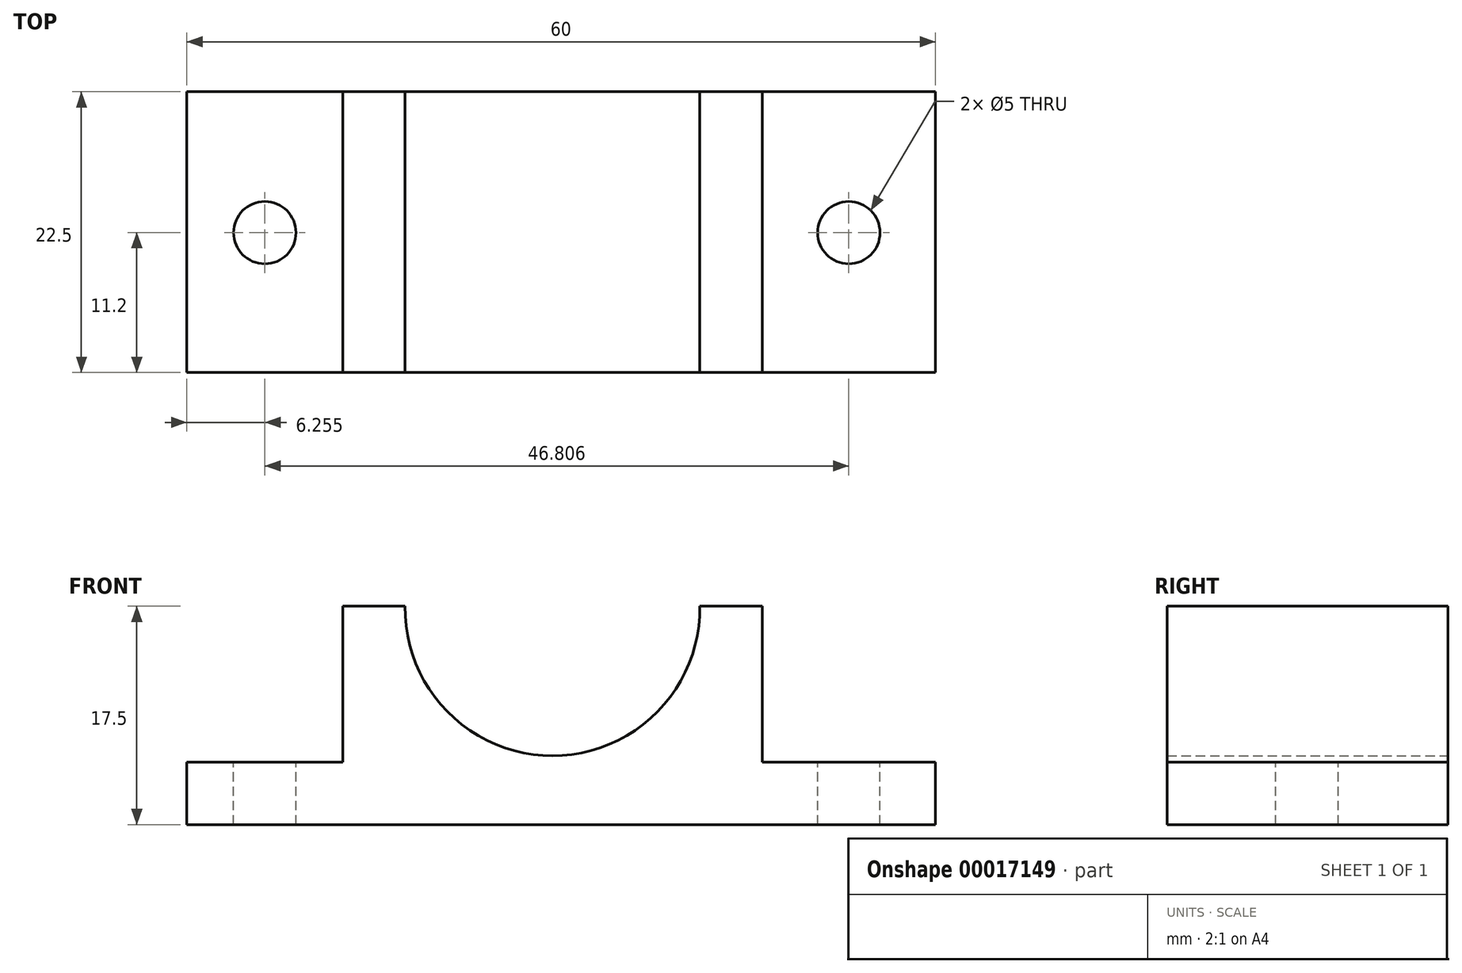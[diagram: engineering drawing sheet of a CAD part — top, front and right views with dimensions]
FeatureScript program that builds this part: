
annotation { "Feature Type Name" : "Feature", "Feature Type Description" : "" }
export const myFeature = defineFeature(function(context is Context, id is Id, definition is map)
    precondition{}
    {
        {
            var Q0;
            Q0=qCreatedBy(makeId("Front.planeOp"),FACE);
            var sketch = newSketch(context, id + "F0", { "sketchPlane" : qUnion([Q0])});
            skLineSegment(sketch, "E0", {"start": v(-45.96, -17.5) * mm, "end": v(14.04, -17.5) * mm});
            skLineSegment(sketch, "E1", {"start": v(14.04, -17.5) * mm, "end": v(14.04, -12.5) * mm});
            skLineSegment(sketch, "E2", {"start": v(14.04, -12.5) * mm, "end": v(0.16, -12.5) * mm});
            skLineSegment(sketch, "E3", {"start": v(0.16, -12.5) * mm, "end": v(0.16, 0) * mm});
            skLineSegment(sketch, "E4", {"start": v(0.16, 0) * mm, "end": v(-4.84, 0) * mm});
            skLineSegment(sketch, "E5", {"start": v(-45.96, -17.5) * mm, "end": v(-45.96, -12.5) * mm});
            skLineSegment(sketch, "E6", {"start": v(-45.96, -12.5) * mm, "end": v(-33.46, -12.5) * mm});
            skLineSegment(sketch, "E7", {"start": v(-33.46, -12.5) * mm, "end": v(-33.46, 0) * mm});
            skLineSegment(sketch, "E8", {"start": v(-33.46, 0) * mm, "end": v(-28.46, 0) * mm});
            skArc(sketch, "E9", {"start": v(-28.46, 0) * mm, "mid": v(-16.65, -11.99) * mm, "end": v(-4.84, 0) * mm});
            skSolve(sketch);
        }
        {
            var Q0;
            Q0=makeQuery(id+"F0.imprint","IMPRINT",FACE,{"disambiguationData":[TD([[makeQuery(id+"F0.imprint","IMPRINT",EDGE,{"derivedFrom":sQuery(id+"F0.wireOp",EDGE,"E0")}),1.0]])]});
            extrude(context, id + "F1", {"entities" : qUnion([Q0]), "depth" : 22.5 * mm});
        }
        {
            var Q0;
            Q0=makeQuery(id+"F1.opExtrude","SWEPT_FACE",FACE,{"disambiguationData":[OSD([sQuery(id+"F0.wireOp",EDGE,"E6")])]});
            var sketch = newSketch(context, id + "F2", { "sketchPlane" : qUnion([Q0])});
            skCircle(sketch, "E10", {"center": v(-39.7, -11.3) * mm, "radius": 2.5 * mm});
            skSolve(sketch);
        }
        {
            var Q0;
            Q0=makeQuery(id+"F1.opExtrude","SWEPT_FACE",FACE,{"disambiguationData":[OSD([sQuery(id+"F0.wireOp",EDGE,"E2")])]});
            var sketch = newSketch(context, id + "F3", { "sketchPlane" : qUnion([Q0])});
            skCircle(sketch, "E11", {"center": v(7.1, -11.3) * mm, "radius": 2.5 * mm});
            skSolve(sketch);
        }
        {
            var Q0;
            Q0=makeQuery(id+"F2.imprint","IMPRINT",FACE,{"disambiguationData":[TD([[makeQuery(id+"F2.imprint","IMPRINT",EDGE,{"derivedFrom":sQuery(id+"F2.wireOp",EDGE,"E10")}),1.0]])]});
            var Q1;
            Q1=makeQuery(id+"F3.imprint","IMPRINT",FACE,{"disambiguationData":[TD([[makeQuery(id+"F3.imprint","IMPRINT",EDGE,{"derivedFrom":sQuery(id+"F3.wireOp",EDGE,"E11")}),1.0]])]});
            extrude(context, id + "F4", {"entities" : qUnion([Q0, Q1]), "operationType" : NewBodyOperationType.REMOVE, "endBound" : BoundingType.THROUGH_ALL, "oppositeDirection" : true, "depth" : 25 * mm});
        }
    });
